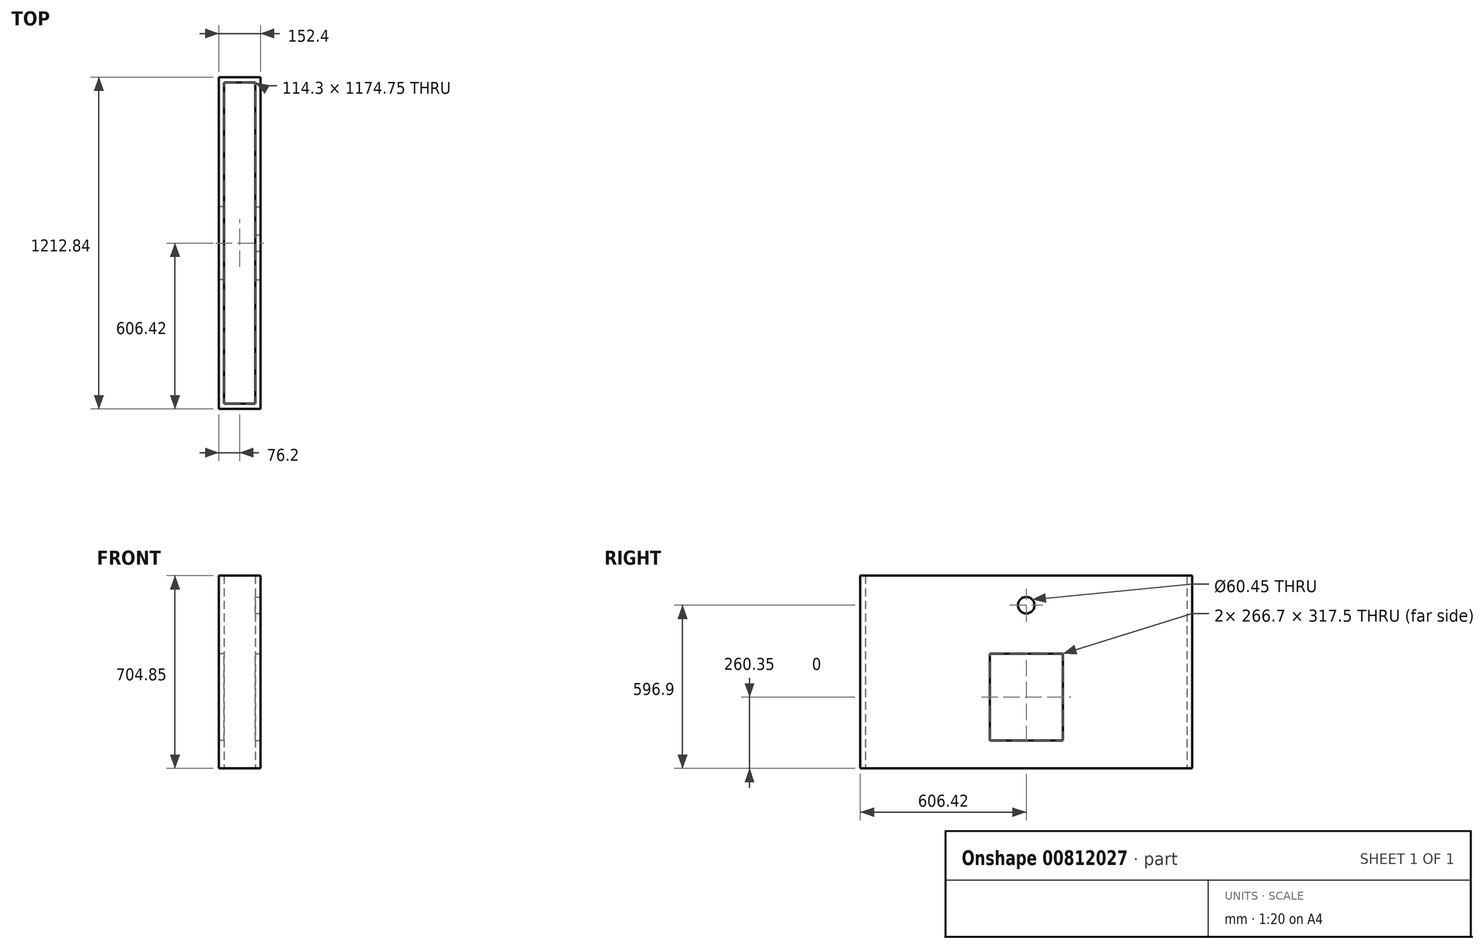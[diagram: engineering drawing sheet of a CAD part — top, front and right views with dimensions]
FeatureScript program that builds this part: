
annotation { "Feature Type Name" : "Feature", "Feature Type Description" : "" }
export const myFeature = defineFeature(function(context is Context, id is Id, definition is map)
    precondition{}
    {
        {
            var Q0;
            Q0=qCreatedBy(makeId("Top.planeOp"),FACE);
            var sketch = newSketch(context, id + "F0", { "sketchPlane" : qUnion([Q0])});
            skLineSegment(sketch, "E0.bottom", {"start": v(76.2, 606.43) * mm, "end": v(-76.2, 606.43) * mm});
            skLineSegment(sketch, "E0.top", {"start": v(76.2, -606.43) * mm, "end": v(-76.2, -606.43) * mm});
            skLineSegment(sketch, "E0.left", {"start": v(76.2, 606.43) * mm, "end": v(76.2, -606.43) * mm});
            skLineSegment(sketch, "E0.right", {"start": v(-76.2, 606.43) * mm, "end": v(-76.2, -606.43) * mm});
            skPoint(sketch, "E0.middle", {"position": v(0, 0) * mm});
            skLineSegment(sketch, "E1.bottom", {"start": v(57.15, 587.38) * mm, "end": v(-57.15, 587.38) * mm});
            skLineSegment(sketch, "E1.top", {"start": v(57.15, -587.38) * mm, "end": v(-57.15, -587.38) * mm});
            skLineSegment(sketch, "E1.left", {"start": v(57.15, 587.38) * mm, "end": v(57.15, -587.38) * mm});
            skLineSegment(sketch, "E1.right", {"start": v(-57.15, 587.38) * mm, "end": v(-57.15, -587.38) * mm});
            skSolve(sketch);
        }
        {
            var Q0;
            Q0=makeQuery(id+"F0.imprint","IMPRINT",FACE,{"disambiguationData":[TD([[makeQuery(id+"F0.imprint","IMPRINT",EDGE,{"derivedFrom":sQuery(id+"F0.wireOp",EDGE,"E0.bottom")}),1.0]])]});
            extrude(context, id + "F1", {"entities" : qUnion([Q0]), "depth" : 704.85 * mm, "offsetDistance" : 25.4 * mm});
        }
        {
            var Q0;
            Q0=makeQuery(id+"F1.opExtrude","SWEPT_FACE",FACE,{"disambiguationData":[OSD([sQuery(id+"F0.wireOp",EDGE,"E0.left")])]});
            var sketch = newSketch(context, id + "F2", { "sketchPlane" : qUnion([Q0])});
            skLineSegment(sketch, "E2", {"start": v(0, 0) * mm, "end": v(0, 101.6) * mm});
            skPoint(sketch, "E2.endSnap0", {"position": v(0, 0) * mm});
            skLineSegment(sketch, "E3", {"start": v(0, 101.6) * mm, "end": v(0, 260.35) * mm});
            skLineSegment(sketch, "E4.bottom", {"start": v(133.35, 101.6) * mm, "end": v(-133.35, 101.6) * mm});
            skLineSegment(sketch, "E4.top", {"start": v(133.35, 419.1) * mm, "end": v(-133.35, 419.1) * mm});
            skLineSegment(sketch, "E4.left", {"start": v(133.35, 101.6) * mm, "end": v(133.35, 419.1) * mm});
            skLineSegment(sketch, "E4.right", {"start": v(-133.35, 101.6) * mm, "end": v(-133.35, 419.1) * mm});
            skPoint(sketch, "E4.middle", {"position": v(0, 260.35) * mm});
            skLineSegment(sketch, "E5", {"start": v(0, 419.1) * mm, "end": v(0, 596.9) * mm});
            skPoint(sketch, "E5.endSnap0", {"position": v(0, 419.1) * mm});
            skCircle(sketch, "E6", {"center": v(0, 596.9) * mm, "radius": 30.23 * mm});
            skPoint(sketch, "E7.endSnap0", {"position": v(0, 704.85) * mm});
            skSolve(sketch);
        }
        {
            var Q0;
            Q0=makeQuery(id+"F2.imprint","IMPRINT",FACE,{"disambiguationData":[TD([[makeQuery(id+"F2.imprint","IMPRINT",EDGE,{"derivedFrom":sQuery(id+"F2.wireOp",EDGE,"GGn8ku5c-GKVz-RgPz-p5no-ucrrB1cT99kD")}),1.0]])]});
            var Q1;
            Q1=makeQuery(id+"F2.imprint","IMPRINT",FACE,{"disambiguationData":[TD([[makeQuery(id+"F2.imprint","IMPRINT",EDGE,{"derivedFrom":sQuery(id+"F2.wireOp",EDGE,"E6")}),1.0]])]});
            var Q2;
            {var subQ3=sQuery(id+"F2.wireOp",EDGE,"E4.left");Q2=makeQuery(id+"F2.imprint","IMPRINT",FACE,{"disambiguationData":[TD([[makeQuery(id+"F2.imprint","IMPRINT",EDGE,{"derivedFrom":subQ3}),1.0]])]});}
            extrude(context, id + "F3", {"entities" : qUnion([Q0, Q1, Q2]), "operationType" : NewBodyOperationType.REMOVE, "oppositeDirection" : true, "depth" : 25.4 * mm, "offsetDistance" : 25.4 * mm});
        }
        {
            var Q0;
            Q0=makeQuery(id+"F1.opExtrude","SWEPT_FACE",FACE,{"disambiguationData":[OSD([sQuery(id+"F0.wireOp",EDGE,"E0.right")])]});
            var sketch = newSketch(context, id + "F4", { "sketchPlane" : qUnion([Q0])});
            skLineSegment(sketch, "E8", {"start": v(0, 0) * mm, "end": v(0, 101.6) * mm});
            skLineSegment(sketch, "E9", {"start": v(0, 101.6) * mm, "end": v(0, 260.35) * mm});
            skLineSegment(sketch, "E10.bottom", {"start": v(133.35, 101.6) * mm, "end": v(-133.35, 101.6) * mm});
            skLineSegment(sketch, "E10.top", {"start": v(133.35, 419.1) * mm, "end": v(-133.35, 419.1) * mm});
            skLineSegment(sketch, "E10.left", {"start": v(133.35, 101.6) * mm, "end": v(133.35, 419.1) * mm});
            skLineSegment(sketch, "E10.right", {"start": v(-133.35, 101.6) * mm, "end": v(-133.35, 419.1) * mm});
            skPoint(sketch, "E10.middle", {"position": v(0, 260.35) * mm});
            skSolve(sketch);
        }
        {
            var Q0;
            Q0=makeQuery(id+"F4.imprint","IMPRINT",FACE,{"disambiguationData":[TD([[makeQuery(id+"F4.imprint","IMPRINT",EDGE,{"derivedFrom":sQuery(id+"F4.wireOp",EDGE,"E10.top")}),1.0]])]});
            extrude(context, id + "F5", {"entities" : qUnion([Q0]), "operationType" : NewBodyOperationType.REMOVE, "oppositeDirection" : true, "depth" : 19.05 * mm, "offsetDistance" : 25.4 * mm});
        }
    });
